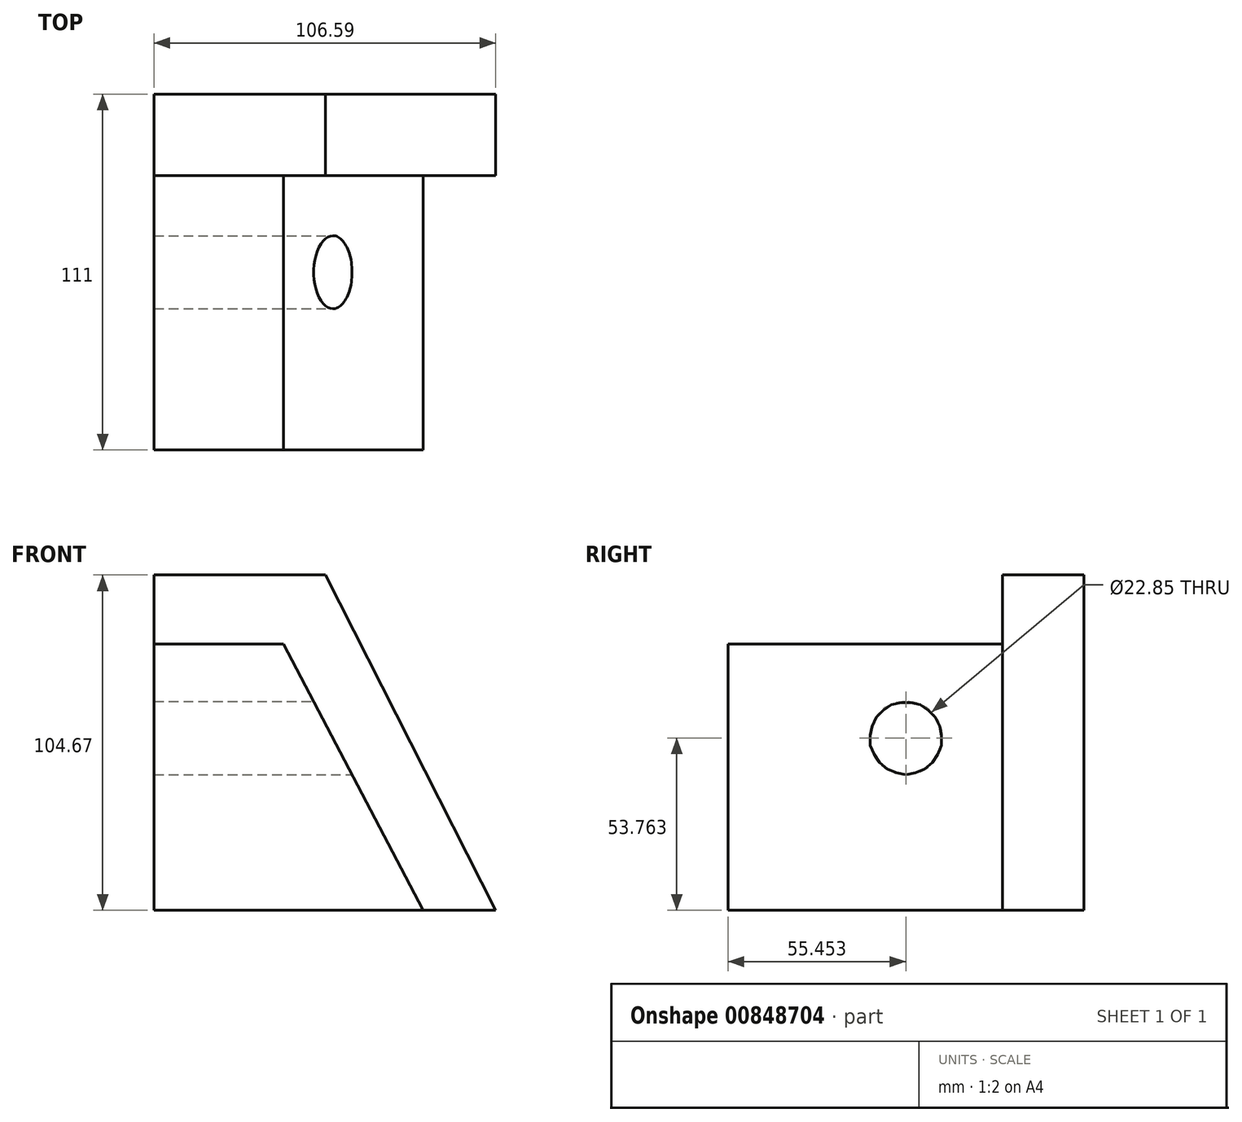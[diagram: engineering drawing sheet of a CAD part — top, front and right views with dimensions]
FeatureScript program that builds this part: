
annotation { "Feature Type Name" : "Feature", "Feature Type Description" : "" }
export const myFeature = defineFeature(function(context is Context, id is Id, definition is map)
    precondition{}
    {
        {
            var Q0;
            Q0=qCreatedBy(makeId("Front.planeOp"),FACE);
            var sketch = newSketch(context, id + "F0", { "sketchPlane" : qUnion([Q0])});
            skLineSegment(sketch, "E0", {"start": v(0, 0) * mm, "end": v(-83.97, 0) * mm});
            skLineSegment(sketch, "E1", {"start": v(-83.97, 0) * mm, "end": v(-83.97, 83.08) * mm});
            skLineSegment(sketch, "E2", {"start": v(-83.97, 83.08) * mm, "end": v(-43.57, 83.08) * mm});
            skLineSegment(sketch, "E3", {"start": v(-43.57, 83.08) * mm, "end": v(0, 0) * mm});
            skSolve(sketch);
        }
        {
            var Q0;
            Q0 = qSketchRegion(id + "F0", true);
            extrude(context, id + "F1", {"entities" : qUnion([Q0]), "depth" : 85.6 * mm, "offsetDistance" : 25.4 * mm});
        }
        {
            var Q0;
            Q0=makeQuery(id+"F1.opExtrude","CAP_FACE",FACE,{"disambiguationData":[OSD([sQuery(id+"F0.wireOp",EDGE,"E0"),sQuery(id+"F0.wireOp",EDGE,"E1"),sQuery(id+"F0.wireOp",EDGE,"E2"),sQuery(id+"F0.wireOp",EDGE,"E3")])],"isStart":true});
            var sketch = newSketch(context, id + "F2", { "sketchPlane" : qUnion([Q0])});
            skLineSegment(sketch, "E4", {"start": v(83.97, 0) * mm, "end": v(-22.62, 0) * mm});
            skLineSegment(sketch, "E5", {"start": v(-22.62, 0) * mm, "end": v(30.5, 104.67) * mm});
            skLineSegment(sketch, "E6", {"start": v(30.5, 104.67) * mm, "end": v(83.97, 104.67) * mm});
            skLineSegment(sketch, "E7", {"start": v(83.97, 104.67) * mm, "end": v(83.97, 0) * mm});
            skSolve(sketch);
        }
        {
            var Q0;
            Q0 = qSketchRegion(id + "F2", true);
            extrude(context, id + "F3", {"entities" : qUnion([Q0]), "operationType" : NewBodyOperationType.ADD, "depth" : 25.4 * mm, "offsetDistance" : 25.4 * mm});
        }
        {
            var Q0;
            Q0=qCreatedBy(makeId("Right.planeOp"),FACE);
            var sketch = newSketch(context, id + "F4", { "sketchPlane" : qUnion([Q0])});
            skCircle(sketch, "E8", {"center": v(-30.15, 53.76) * mm, "radius": 11.43 * mm});
            skSolve(sketch);
        }
        {
            var Q0;
            Q0 = qSketchRegion(id + "F4", true);
            extrude(context, id + "F5", {"entities" : qUnion([Q0]), "operationType" : NewBodyOperationType.REMOVE, "endBound" : BoundingType.THROUGH_ALL, "oppositeDirection" : true, "depth" : 25.4 * mm, "offsetDistance" : 25.4 * mm});
        }
    });
